# Revit family: E_Actuator_F_MEPcontent_Oventrop_Aktor M ST 3P L
name_source: partatom
category: Electrical Fixtures
revit_build: Autodesk Revit MEP 2015 (Build: 20140606_1530(x64)
units: mm (PartAtom-declared; Revit-internal decimal feet)

## types (3) — shared parameters
Ambient Temperature = 0 °C up to 50 °C
Black = Color RGB 060-060-060
Content Supplier URL = www.mepcontent.eu
Custom = No
Default Elevation = 1219.2 mm  [stored 4 ft]
EMCS Version = 2.0
ETIM Article Class = EC011290
Family Version = 10.14
Grey = Color RGB 100-100-100
Height = 242 mm  [stored 0.793963 ft]
IFCExportAs = IfcActuatorType
IFCExportType = ELECTRICACTUATOR
Length = 145 mm  [stored 0.475722 ft]
MEPcontent Class = ACTUATOR
Manufacturer = Oventrop
Manufacturer URL = http://www.oventrop.com
Max. Fluid Temperature = 120 °C
Max. Piston Stroke = 20 mm
Product Line = Oventrop
Protection = IP 54 according to EN 60529
Revit Version = 2015
Storage Temperature = 0 °C up to 50 °C
URL = www.stabiplan.com
Voltage = 24 V
White = Color RGB 245-245-245
Width = 95 mm

## per-type parameters (varying)
| type | Actuator | Article Description | Description | Drive | Emergency Setting Time | Floating Time | GTIN | Manufacturer Art. No. | Operating Power | Power Consumption | Steady Control | Steady Control With Pull Back Spring |
| 8020 | reversible synchronous motor | Electromotive actuator "Aktor M" "ST/3P L", 24 V, for Cocon QTR/QFC" DN40 - DN100, with adapter | Electromotive actuator "Aktor M" "ST/3P L", 24 V, for Cocon QTR/QFC" DN40 - DN100, with adapter | 0 - 10 V |  | 9 s / mm | 4026755409147 | 1158020 | 800 N | 4.8 W | Yes | No |
| 8021 | brushless direct current motor | Electromotive actuator "Aktor M" "ST/3P L", 24 V, for Cocon QTR/QFC" DN40 - DN100, opening with current off | Electromotive actuator "Aktor M" "ST/3P L", 24 V, for Cocon QTR/QFC" DN40 - DN100, opening with current off | 0-10 V or 4-20 mA | 1 s / mm | 2 s / mm | 4026755409154 | 1158021 | 1000 N | 26 W | No | Yes |
| 8022 | brushless direct current motor | Electromotive actuator "Aktor M" "ST/3P L", 24 V, for Cocon QTR/QFC" DN40 - DN100, closing with current off | Electromotive actuator "Aktor M" "ST/3P L", 24 V, for Cocon QTR/QFC" DN40 - DN100, closing with current off | 0-10 V or 4-20 mA | 1 s / mm | 2 s / mm | 4026755409161 | 1158022 | 1000 N | 26 W | No | Yes |

note: column(s) folded — value = type name in every type: Article Type, Model

note: [stored X ft] marks values corroborated as IEEE doubles in the binary element streams (Revit-internal decimal feet)

## geometry (parser evidence)
native form markers: Sweep x2
no freeform markers — native parametric forms only
